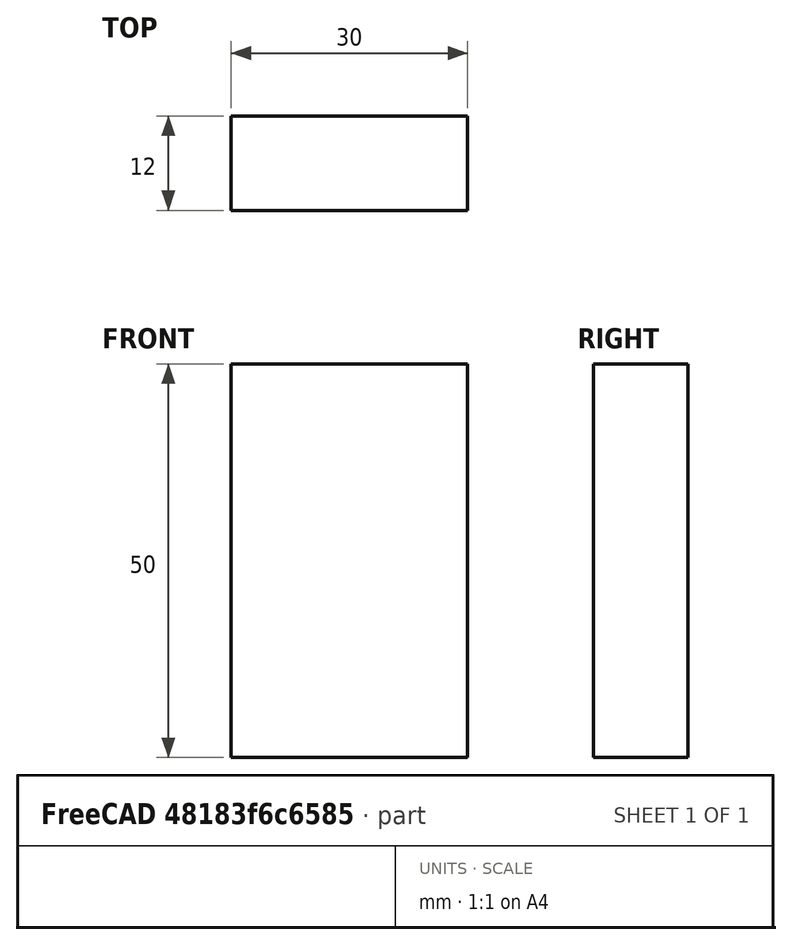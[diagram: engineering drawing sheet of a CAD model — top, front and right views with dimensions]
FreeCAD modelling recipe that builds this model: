
FCSTD DOCUMENT  (FreeCAD 0.15R4671 (Git))
Label: Flat Bar 30x12 EN10058 S235JR
License: All rights reserved
LicenseURL: http://en.wikipedia.org/wiki/All_rights_reserved
objects: Sketcher::SketchObject×1, Part::Extrusion×1
note: 2 computed .brp shape members not serialized (recipe doc carries the construction recipe); baked Part::Feature solids carry a one-line shape summary decoded from their .brp

FEATURE [Sketcher::SketchObject] Sketch
  sketch-geometry (4):
    g0: LineSegment StartX=-15 StartY=-6 StartZ=0 EndX=15 EndY=-6 EndZ=0
    g1: LineSegment StartX=15 StartY=-6 StartZ=0 EndX=15 EndY=6 EndZ=0
    g2: LineSegment StartX=15 StartY=6 StartZ=0 EndX=-15 EndY=6 EndZ=0
    g3: LineSegment StartX=-15 StartY=6 StartZ=0 EndX=-15 EndY=-6 EndZ=0
  constraints (12):
    c: Coincident(g0,g1)
    c: Coincident(g1,g2)
    c: Coincident(g2,g3)
    c: Coincident(g3,g0)
    c: Horizontal(g0)
    c: Horizontal(g2)
    c: Vertical(g1)
    c: Vertical(g3)
    c: Symmetric(g1,g2,g-2)
    c: Symmetric(g0,g1,g-1)
    c: DistanceY(g1) = 12
    c: DistanceX(g0) = 30
FEATURE [Part::Extrusion] Extrude  label="Flat Bar 30x12 EN10058 S235JR"
  Base = -> Sketch
  Dir = (0,0,50)
  Solid = true
